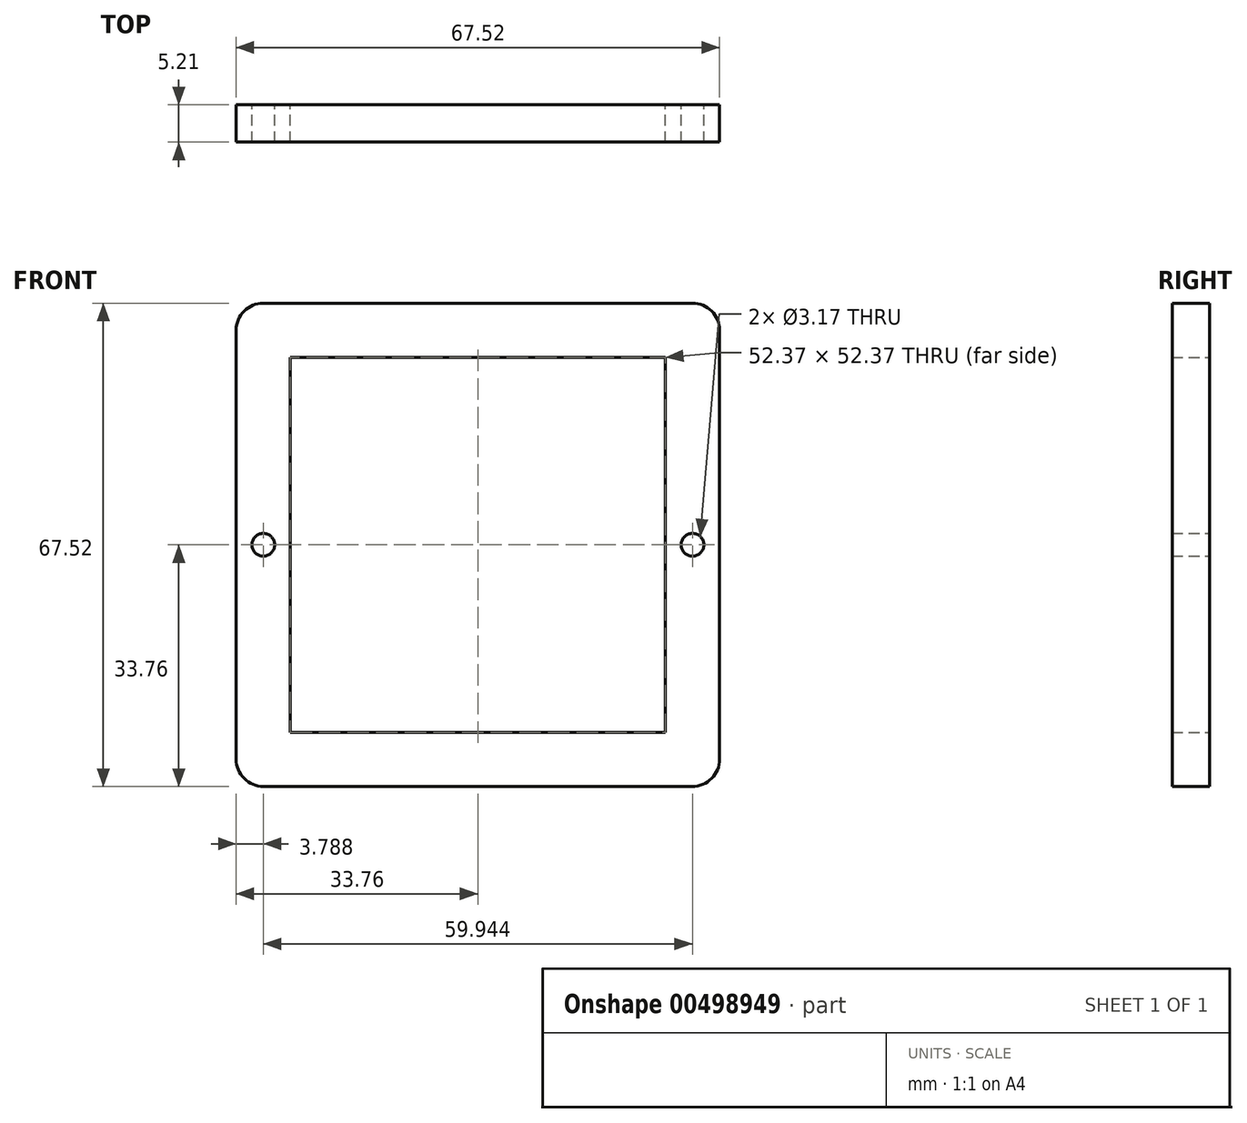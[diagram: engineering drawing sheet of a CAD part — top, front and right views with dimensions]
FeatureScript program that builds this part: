
annotation { "Feature Type Name" : "Feature", "Feature Type Description" : "" }
export const myFeature = defineFeature(function(context is Context, id is Id, definition is map)
    precondition{}
    {
        {
            var Q0;
            Q0=qCreatedBy(makeId("Front.planeOp"),FACE);
            var sketch = newSketch(context, id + "F0", { "sketchPlane" : qUnion([Q0])});
            skLineSegment(sketch, "E0.bottom", {"start": v(26.19, -26.19) * mm, "end": v(-26.19, -26.19) * mm});
            skLineSegment(sketch, "E0.top", {"start": v(26.19, 26.19) * mm, "end": v(-26.19, 26.19) * mm});
            skLineSegment(sketch, "E0.left", {"start": v(26.19, -26.19) * mm, "end": v(26.19, 26.19) * mm});
            skLineSegment(sketch, "E0.right", {"start": v(-26.19, -26.19) * mm, "end": v(-26.19, 26.19) * mm});
            skPoint(sketch, "E0.middle", {"position": v(0, 0) * mm});
            skCircle(sketch, "E1", {"center": v(-29.97, 0) * mm, "radius": 1.59 * mm});
            skCircle(sketch, "E2", {"center": v(29.97, 0) * mm, "radius": 1.59 * mm});
            skLineSegment(sketch, "E3.bottom", {"start": v(29.95, -33.76) * mm, "end": v(-29.95, -33.76) * mm});
            skLineSegment(sketch, "E3.top", {"start": v(29.95, 33.76) * mm, "end": v(-29.95, 33.76) * mm});
            skLineSegment(sketch, "E3.left", {"start": v(33.76, -29.95) * mm, "end": v(33.76, 29.95) * mm});
            skLineSegment(sketch, "E3.right", {"start": v(-33.76, -29.95) * mm, "end": v(-33.76, 29.95) * mm});
            skPoint(sketch, "E4.visualSharp", {"position": v(-33.76, 33.76) * mm});
            skArc(sketch, "E4.filletArc", {"start": v(-29.95, 33.76) * mm, "mid": v(-32.64, 32.64) * mm, "end": v(-33.76, 29.95) * mm});
            skPoint(sketch, "E5.visualSharp", {"position": v(33.76, 33.76) * mm});
            skArc(sketch, "E5.filletArc", {"start": v(33.76, 29.95) * mm, "mid": v(32.64, 32.64) * mm, "end": v(29.95, 33.76) * mm});
            skPoint(sketch, "E6.visualSharp", {"position": v(33.76, -33.76) * mm});
            skArc(sketch, "E6.filletArc", {"start": v(29.95, -33.76) * mm, "mid": v(32.64, -32.64) * mm, "end": v(33.76, -29.95) * mm});
            skPoint(sketch, "E7.visualSharp", {"position": v(-33.76, -33.76) * mm});
            skArc(sketch, "E7.filletArc", {"start": v(-33.76, -29.95) * mm, "mid": v(-32.64, -32.64) * mm, "end": v(-29.95, -33.76) * mm});
            skLineSegment(sketch, "E8", {"start": v(-29.97, 0) * mm, "end": v(29.97, 0) * mm, "construction": true});
            skLineSegment(sketch, "E9", {"start": v(-26.19, 26.19) * mm, "end": v(26.19, -26.19) * mm, "construction": true});
            skLineSegment(sketch, "E10.bottom", {"start": v(-22.09, 26.19) * mm, "end": v(26.19, -22.09) * mm, "construction": true});
            skLineSegment(sketch, "E10.top", {"start": v(-26.19, 22.09) * mm, "end": v(22.09, -26.19) * mm, "construction": true});
            skLineSegment(sketch, "E10.left", {"start": v(-22.09, 26.19) * mm, "end": v(-26.19, 22.09) * mm, "construction": true});
            skLineSegment(sketch, "E10.right", {"start": v(26.19, -22.09) * mm, "end": v(22.09, -26.19) * mm, "construction": true});
            skLineSegment(sketch, "E11", {"start": v(26.19, 0) * mm, "end": v(33.76, 0) * mm, "construction": true});
            skSolve(sketch);
        }
        {
            var Q0;
            Q0 = qSketchRegion(id + "F0", true);
            extrude(context, id + "F1", {"entities" : qUnion([Q0]), "depth" : 5.2 * mm});
        }
    });
